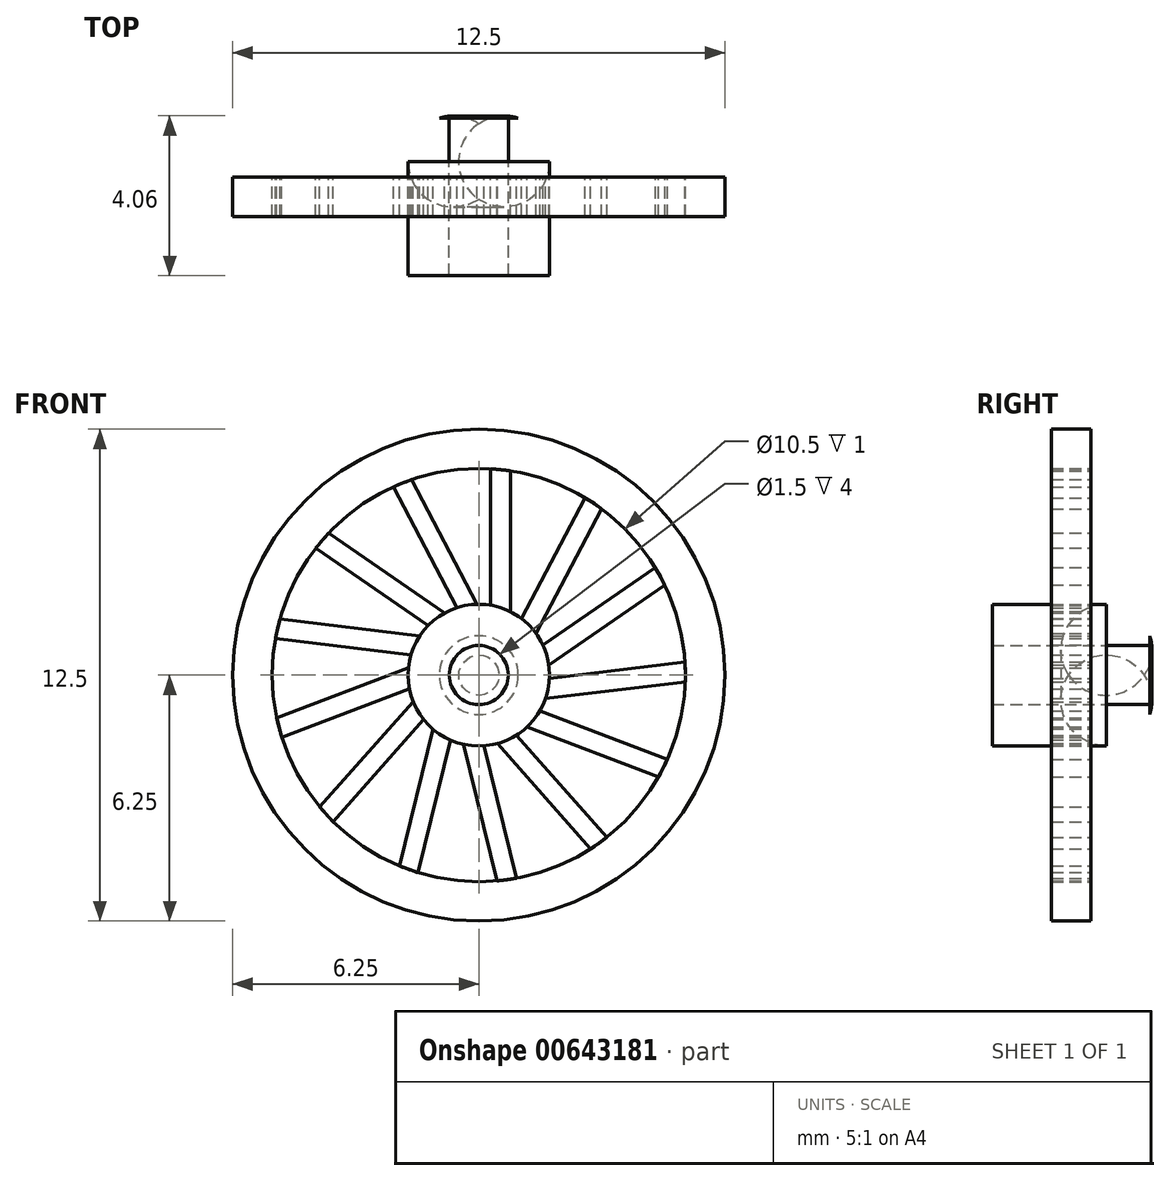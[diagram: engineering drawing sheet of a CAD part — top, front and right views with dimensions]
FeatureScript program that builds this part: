
annotation { "Feature Type Name" : "Feature", "Feature Type Description" : "" }
export const myFeature = defineFeature(function(context is Context, id is Id, definition is map)
    precondition{}
    {
        {
            var Q0;
            Q0=qCreatedBy(makeId("Front.planeOp"),FACE);
            var sketch = newSketch(context, id + "F0", { "sketchPlane" : qUnion([Q0])});
            skCircle(sketch, "E0", {"center": v(0, 0) * mm, "radius": 6.25 * mm});
            skCircle(sketch, "E1", {"center": v(0, 0) * mm, "radius": 5.25 * mm});
            skCircle(sketch, "E2", {"center": v(0, 0) * mm, "radius": 1.8 * mm});
            skLineSegment(sketch, "E3", {"start": v(0.3, 5.24) * mm, "end": v(0.3, 1.77) * mm});
            skLineSegment(sketch, "E4", {"start": v(0.8, 5.19) * mm, "end": v(0.8, 1.61) * mm});
            skArc(sketch, "E5", {"start": v(0.8, 5.19) * mm, "mid": v(0.55, 5.22) * mm, "end": v(0.3, 5.24) * mm});
            skArc(sketch, "E6", {"start": v(0.8, 1.61) * mm, "mid": v(0.56, 1.71) * mm, "end": v(0.3, 1.77) * mm});
            skSolve(sketch);
        }
        {
            var Q0;
            {var subQ0=sQuery(id+"F0.wireOp",EDGE,"E3");Q0=makeQuery(id+"F0.imprint","IMPRINT",FACE,{"disambiguationData":[TD([[makeQuery(id+"F0.imprint","IMPRINT",EDGE,{"derivedFrom":subQ0}),1.0]])]});}
            var Q1;
            Q1=makeQuery(id+"F0.imprint","IMPRINT",FACE,{"disambiguationData":[TD([[makeQuery(id+"F0.imprint","IMPRINT",EDGE,{"derivedFrom":sQuery(id+"F0.wireOp",EDGE,"E0")}),1.0]])]});
            var Q2;
            {var subQ0=sQuery(id+"F0.wireOp",EDGE,"E2");var subQ1=makeQuery(id+"F0.imprint","INTERSECT",VERTEX,{"derivedFrom":[subQ0,sQuery(id+"F0.wireOp",EDGE,"E3")]});Q2=makeQuery(id+"F0.imprint","IMPRINT",FACE,{"disambiguationData":[TD([[makeQuery(id+"F0.imprint","IMPRINT",EDGE,{"disambiguationData":[TD([[subQ1,1.0]])],"derivedFrom":subQ0}),1.0]])]});}
            extrude(context, id + "F1", {"entities" : qUnion([Q0, Q1, Q2]), "depth" : 1 * mm, "offsetDistance" : 25 * mm});
        }
        {
            var Q0;
            Q0=makeQuery(id+"F1.opExtrude","SWEPT_BODY",BODY,{"disambiguationData":[OSD([sQuery(id+"F0.wireOp",EDGE,"E2"),sQuery(id+"F0.wireOp",EDGE,"E3"),sQuery(id+"F0.wireOp",EDGE,"E4"),sQuery(id+"F0.wireOp",EDGE,"E5")])]});
            var Q1;
            Q1=makeQuery(id+"F1.opExtrude","SWEPT_BODY",BODY,{"disambiguationData":[OSD([sQuery(id+"F0.wireOp",EDGE,"E0"),sQuery(id+"F0.wireOp",EDGE,"E1")])]});
            var Q2;
            Q2=makeQuery(id+"F1.opExtrude","SWEPT_FACE",FACE,{"disambiguationData":[OSD([sQuery(id+"F0.wireOp",EDGE,"E2")])]});
            circularPattern(context, id + "F2", {"operationType" : NewBodyOperationType.ADD, "entities" : qUnion([Q0, Q1]), "axis" : qUnion([Q2]), "angle" : 360 * degree, "instanceCount" : 13, "equalSpace" : true});
        }
        {
            var Q0;
            Q0=qCreatedBy(makeId("Right.planeOp"),FACE);
            var sketch = newSketch(context, id + "F3", { "sketchPlane" : qUnion([Q0])});
            skLineSegment(sketch, "E7", {"start": v(0, 0) * mm, "end": v(3.16, 0) * mm, "construction": true});
            skLineSegment(sketch, "E8", {"start": v(0, 0) * mm, "end": v(0, 1.8) * mm});
            skLineSegment(sketch, "E9", {"start": v(0, 1.8) * mm, "end": v(0.4, 1.8) * mm});
            skLineSegment(sketch, "E10", {"start": v(1.5, 1) * mm, "end": v(1.5, 0) * mm});
            skArc(sketch, "E11", {"start": v(1.5, 1) * mm, "mid": v(1.08, 1.58) * mm, "end": v(0.4, 1.8) * mm});
            skLineSegment(sketch, "E12", {"start": v(0, 0) * mm, "end": v(1.5, 0) * mm});
            skSolve(sketch);
        }
        {
            var Q0;
            Q0=makeQuery(id+"F3.imprint","IMPRINT",FACE,{"disambiguationData":[TD([[makeQuery(id+"F3.imprint","IMPRINT",EDGE,{"derivedFrom":sQuery(id+"F3.wireOp",EDGE,"E8")}),-1.0]])]});
            var Q1;
            Q1=sQuery(id+"F3.wireOp",EDGE,"E7");
            revolve(context, id + "F4", {"operationType" : NewBodyOperationType.ADD, "entities" : qUnion([Q0]), "axis" : qUnion([Q1]), "revolveType" : RevolveType.FULL});
        }
        {
            var Q0;
            {var subQ0=makeQuery(id+"F1.opExtrude","CAP_FACE",FACE,{"disambiguationData":[OSD([sQuery(id+"F0.wireOp",EDGE,"E2"),sQuery(id+"F0.wireOp",EDGE,"E3"),sQuery(id+"F0.wireOp",EDGE,"E4"),sQuery(id+"F0.wireOp",EDGE,"E5")])],"isStart":false});Q0=makeQuery(id+"F2.boolean.opBoolean","MERGE",FACE,{"derivedFrom":[subQ0,makeQuery(id+"F2.opPattern","COPY",FACE,{"derivedFrom":subQ0,"instanceName":"1"}),makeQuery(id+"F2.opPattern","COPY",FACE,{"derivedFrom":subQ0,"instanceName":"2"}),makeQuery(id+"F2.opPattern","COPY",FACE,{"derivedFrom":subQ0,"instanceName":"3"}),makeQuery(id+"F2.opPattern","COPY",FACE,{"derivedFrom":subQ0,"instanceName":"4"}),makeQuery(id+"F2.opPattern","COPY",FACE,{"derivedFrom":subQ0,"instanceName":"5"}),makeQuery(id+"F2.opPattern","COPY",FACE,{"derivedFrom":subQ0,"instanceName":"6"}),makeQuery(id+"F2.opPattern","COPY",FACE,{"derivedFrom":subQ0,"instanceName":"7"}),makeQuery(id+"F2.opPattern","COPY",FACE,{"derivedFrom":subQ0,"instanceName":"8"}),makeQuery(id+"F2.opPattern","COPY",FACE,{"derivedFrom":subQ0,"instanceName":"9"}),makeQuery(id+"F2.opPattern","COPY",FACE,{"derivedFrom":subQ0,"instanceName":"10"}),makeQuery(id+"F2.opPattern","COPY",FACE,{"derivedFrom":subQ0,"instanceName":"11"}),makeQuery(id+"F2.opPattern","COPY",FACE,{"derivedFrom":subQ0,"instanceName":"12"})]});}
            var sketch = newSketch(context, id + "F5", { "sketchPlane" : qUnion([Q0])});
            skCircle(sketch, "E13", {"center": v(0, 0) * mm, "radius": 1.8 * mm});
            skSolve(sketch);
        }
        {
            var Q0;
            Q0=makeQuery(id+"F4.opRevolve","SWEPT_FACE",FACE,{"disambiguationData":[OSD([sQuery(id+"F3.wireOp",EDGE,"E10")])]});
            var sketch = newSketch(context, id + "F6", { "sketchPlane" : qUnion([Q0])});
            skCircle(sketch, "E14", {"center": v(0, 0) * mm, "radius": 0.75 * mm});
            skSolve(sketch);
        }
        {
            var Q0;
            Q0 = qSketchRegion(id + "F5", true);
            extrude(context, id + "F7", {"entities" : qUnion([Q0]), "operationType" : NewBodyOperationType.ADD, "depth" : 1.5 * mm, "offsetDistance" : 25 * mm});
        }
        {
            var Q0;
            Q0 = qSketchRegion(id + "F6", true);
            extrude(context, id + "F8", {"entities" : qUnion([Q0]), "operationType" : NewBodyOperationType.REMOVE, "oppositeDirection" : true, "depth" : 25 * mm, "offsetDistance" : 25 * mm});
        }
    });
